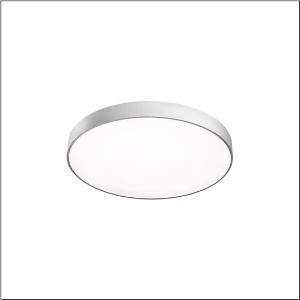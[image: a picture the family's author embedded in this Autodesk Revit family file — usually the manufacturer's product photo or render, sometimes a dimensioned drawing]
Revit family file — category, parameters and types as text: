
# Revit family: round_21_m_51mr36fd0421s
name_source: partatom
category: Lighting Fixtures
units: mm (PartAtom-declared; Revit-internal decimal feet)

## family parameters
Cut with Voids When Loaded = No
Host = Face
Light Source = No
Part Type = Normal
Room Calculation Point = No
Round Connector Dimension = Use Diameter
Shared = No

## types (1)
- Round 21 M (1 x LED, 7810 lm, 54.9 W, 4000K)
    Apparent Load = 55 VA
    CIE Flux Codes = 49 80 96 100 100
    Color Rendering = 80
    Color Temperature = 4000K
    Default Elevation = 1800 mm
    Description = Round 21 M, wall and ceiling luminaire, primary optical cover: cover, of PMMA, opal, light emission: direct distribution, primary light characteristic: symmetric, installation type: surface-mounted, suspended mounting, LED, rated luminous flux: 7.810lm, luminous efficacy: 142lm/W, light colour: 840, colour temperature: 4000K, with terminal, 5-pole, mains connection: 230V, AC, 50/60Hz, rated input power: 55W, housing, of aluminium, coated, silver, diameter: 600mm, height: 62mm, protection rating (complete): IP40, insulation class (complete): insulation class I (protective earthing), certification: CE, impact resistance: IK04, permissible operating ambient temperature: -10..+35°C, packaging unit: 1 piece
    Height = 87 mm
    Lamp = 1 x LED
    Lamp Light Flux = 7810 lm
    Lamp Power = 54.9 W
    Lamp count = 1
    Length = 600 mm
    Luminous efficacy = 142 lm/W
    Manufacturer = Siteco
    ModVariant = No
    Model = 51MR36FD0421S
    Mounting Place = Ceiling
    Mounting Type = Surface mounted
    Number of Poles = 1
    OnlyDefault = Yes
    Power Factor = 1
    Product Name = Round 21 M
    Product group = wall and ceiling luminaire
    ProductGroupID = 303
    Protection Class = Protection class I
    Protection Degree = IP 40
    RLX_Detail_Level = 1
    RLX_Emergency_Light_Flux = 0 lm
    RLX_Emergency_Type = 0
    RLX_Emergency_Type_DB = No
    RlxData = <blob elided: 14789 chars, md5=a98064b6>
    Socket = socket
    Standby Power = 0 W
    System Light Flux = 7810 lm
    System Power = 55 W
    Type Comments = Product without accessories
    Type Image = l_1258303.jpg
    URL = http://relux.com
    VarID = ---
    Voltage = 0 V
    Weight = 0.00 kg
    Width = 0 mm  [stored 0 ft]

note: [stored X ft] marks values corroborated as IEEE doubles in the binary element streams (Revit-internal decimal feet)

## geometry (parser evidence)
native form markers: Sweep x11
no freeform markers — native parametric forms only
